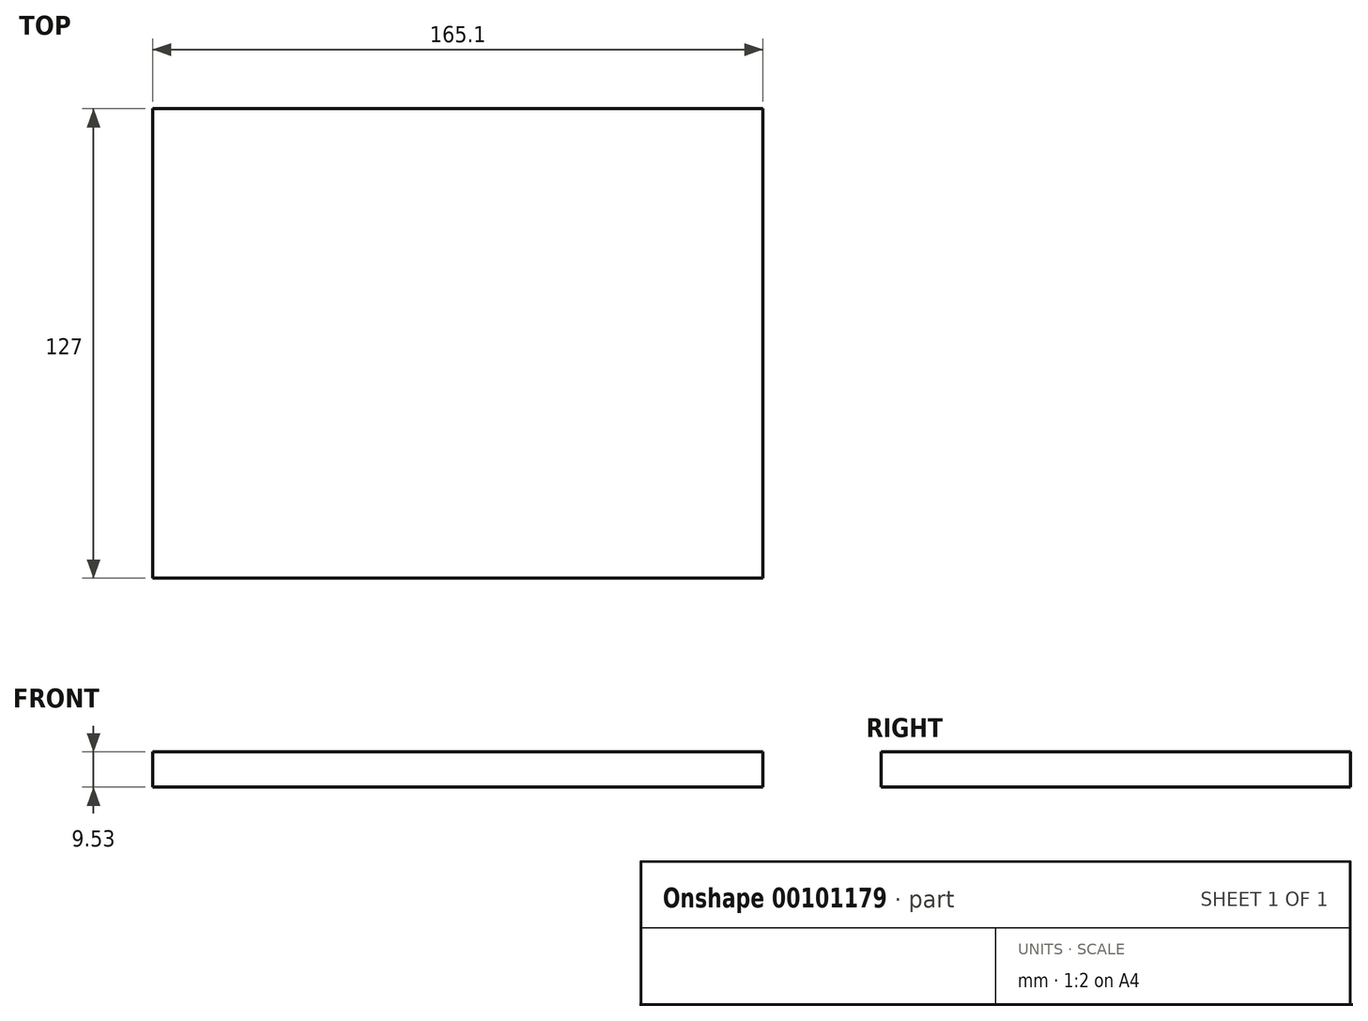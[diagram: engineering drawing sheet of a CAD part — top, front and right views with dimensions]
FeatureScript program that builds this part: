
annotation { "Feature Type Name" : "Feature", "Feature Type Description" : "" }
export const myFeature = defineFeature(function(context is Context, id is Id, definition is map)
    precondition{}
    {
        {
            var Q0;
            Q0=qCreatedBy(makeId("Top.planeOp"),FACE);
            var sketch = newSketch(context, id + "F0", { "sketchPlane" : qUnion([Q0])});
            skLineSegment(sketch, "E0.bottom", {"start": v(82.55, 63.5) * mm, "end": v(-82.55, 63.5) * mm});
            skLineSegment(sketch, "E0.top", {"start": v(82.55, -63.5) * mm, "end": v(-82.55, -63.5) * mm});
            skLineSegment(sketch, "E0.left", {"start": v(82.55, 63.5) * mm, "end": v(82.55, -63.5) * mm});
            skLineSegment(sketch, "E0.right", {"start": v(-82.55, 63.5) * mm, "end": v(-82.55, -63.5) * mm});
            skPoint(sketch, "E0.middle", {"position": v(0, 0) * mm});
            skSolve(sketch);
        }
        {
            var Q0;
            Q0 = qSketchRegion(id + "F0", true);
            extrude(context, id + "F1", {"entities" : qUnion([Q0]), "depth" : 9.52 * mm});
        }
    });
